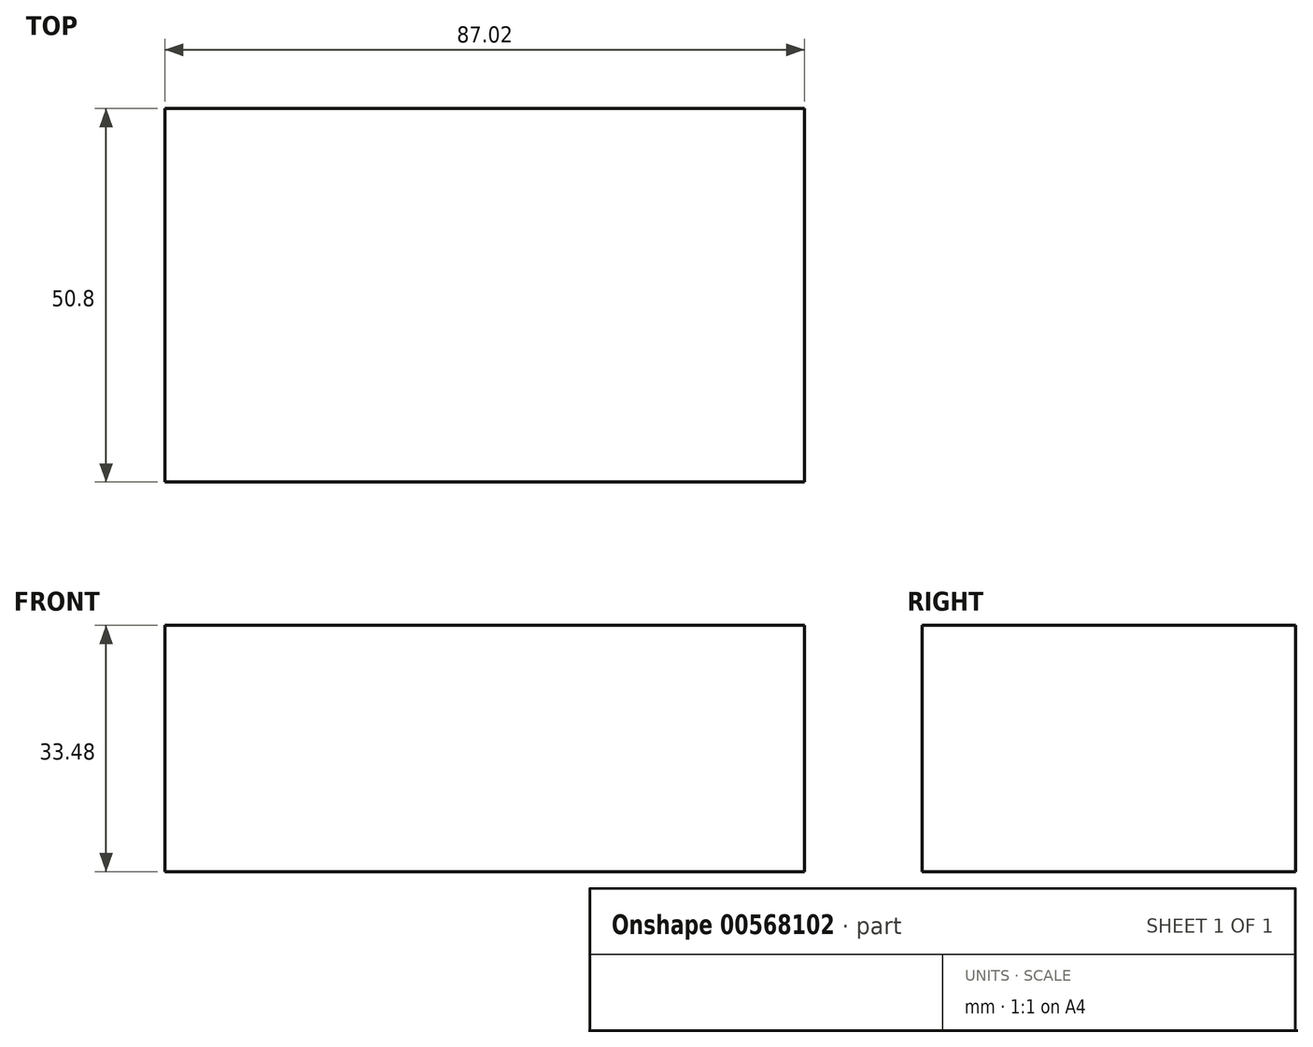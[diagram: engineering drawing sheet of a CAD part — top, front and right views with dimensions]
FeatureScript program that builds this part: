
annotation { "Feature Type Name" : "Feature", "Feature Type Description" : "" }
export const myFeature = defineFeature(function(context is Context, id is Id, definition is map)
    precondition{}
    {
        {
            var Q0;
            Q0=qCreatedBy(makeId("Front.planeOp"),FACE);
            var sketch = newSketch(context, id + "F0", { "sketchPlane" : qUnion([Q0])});
            skLineSegment(sketch, "E0.bottom", {"start": v(0, 0) * mm, "end": v(0, 0) * mm});
            skLineSegment(sketch, "E0.top", {"start": v(0, 0) * mm, "end": v(0, 0) * mm});
            skLineSegment(sketch, "E0.left", {"start": v(0, 0) * mm, "end": v(0, 0) * mm});
            skLineSegment(sketch, "E0.right", {"start": v(0, 0) * mm, "end": v(0, 0) * mm});
            skPoint(sketch, "E0.middle", {"position": v(0, 0) * mm});
            skLineSegment(sketch, "E1.bottom", {"start": v(43.5, 16.74) * mm, "end": v(-43.5, 16.74) * mm});
            skLineSegment(sketch, "E1.top", {"start": v(43.5, -16.74) * mm, "end": v(-43.5, -16.74) * mm});
            skLineSegment(sketch, "E1.left", {"start": v(43.5, 16.74) * mm, "end": v(43.5, -16.74) * mm});
            skLineSegment(sketch, "E1.right", {"start": v(-43.5, 16.74) * mm, "end": v(-43.5, -16.74) * mm});
            skSolve(sketch);
        }
        {
            var Q0;
            Q0=makeQuery(id+"F0.imprint","IMPRINT",FACE,{"disambiguationData":[TD([[makeQuery(id+"F0.imprint","IMPRINT",EDGE,{"derivedFrom":sQuery(id+"F0.wireOp",EDGE,"E1.bottom")}),1.0]])]});
            extrude(context, id + "F1", {"entities" : qUnion([Q0]), "depth" : 25.4 * mm, "offsetDistance" : 25.4 * mm});
        }
        {
            var Q0;
            Q0=makeQuery(id+"F1.opExtrude","CAP_FACE",FACE,{"disambiguationData":[OSD([sQuery(id+"F0.wireOp",EDGE,"E1.bottom"),sQuery(id+"F0.wireOp",EDGE,"E1.top"),sQuery(id+"F0.wireOp",EDGE,"E1.left"),sQuery(id+"F0.wireOp",EDGE,"E1.right")])],"isStart":true});
            extrude(context, id + "F2", {"entities" : qUnion([Q0]), "operationType" : NewBodyOperationType.ADD, "depth" : 25.4 * mm, "offsetDistance" : 25.4 * mm});
        }
    });
